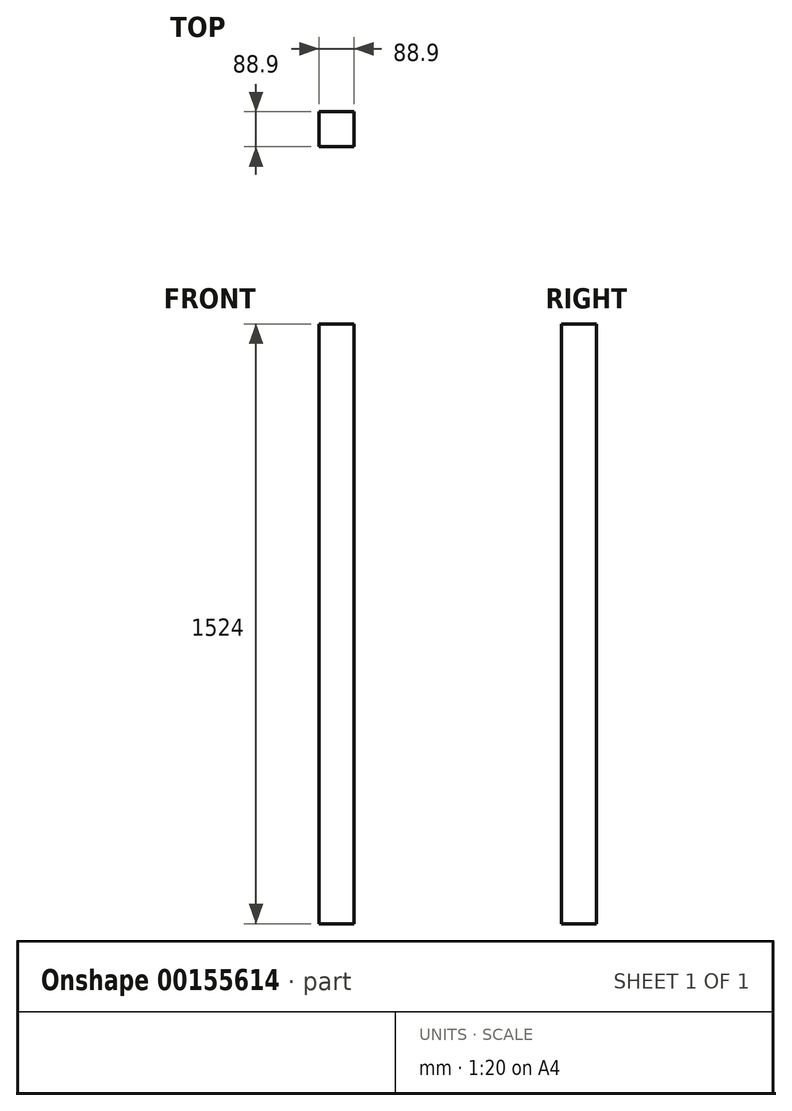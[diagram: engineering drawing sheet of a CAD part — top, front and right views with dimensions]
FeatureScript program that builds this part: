
annotation { "Feature Type Name" : "Feature", "Feature Type Description" : "" }
export const myFeature = defineFeature(function(context is Context, id is Id, definition is map)
    precondition{}
    {
        {
            var Q0;
            Q0=qCreatedBy(makeId("Top.planeOp"),FACE);
            var sketch = newSketch(context, id + "F0", { "sketchPlane" : qUnion([Q0])});
            skLineSegment(sketch, "E0.bottom", {"start": v(-44.45, 44.45) * mm, "end": v(44.45, 44.45) * mm});
            skLineSegment(sketch, "E0.top", {"start": v(-44.45, -44.45) * mm, "end": v(44.45, -44.45) * mm});
            skLineSegment(sketch, "E0.left", {"start": v(-44.45, 44.45) * mm, "end": v(-44.45, -44.45) * mm});
            skLineSegment(sketch, "E0.right", {"start": v(44.45, 44.45) * mm, "end": v(44.45, -44.45) * mm});
            skPoint(sketch, "E0.middle", {"position": v(0, 0) * mm});
            skSolve(sketch);
        }
        {
            var Q0;
            Q0=makeQuery(id+"F0.imprint","IMPRINT",FACE,{"disambiguationData":[TD([[makeQuery(id+"F0.imprint","IMPRINT",EDGE,{"derivedFrom":sQuery(id+"F0.wireOp",EDGE,"E0.bottom")}),-1.0]])]});
            extrude(context, id + "F1", {"entities" : qUnion([Q0]), "depth" : 1524 * mm});
        }
    });
